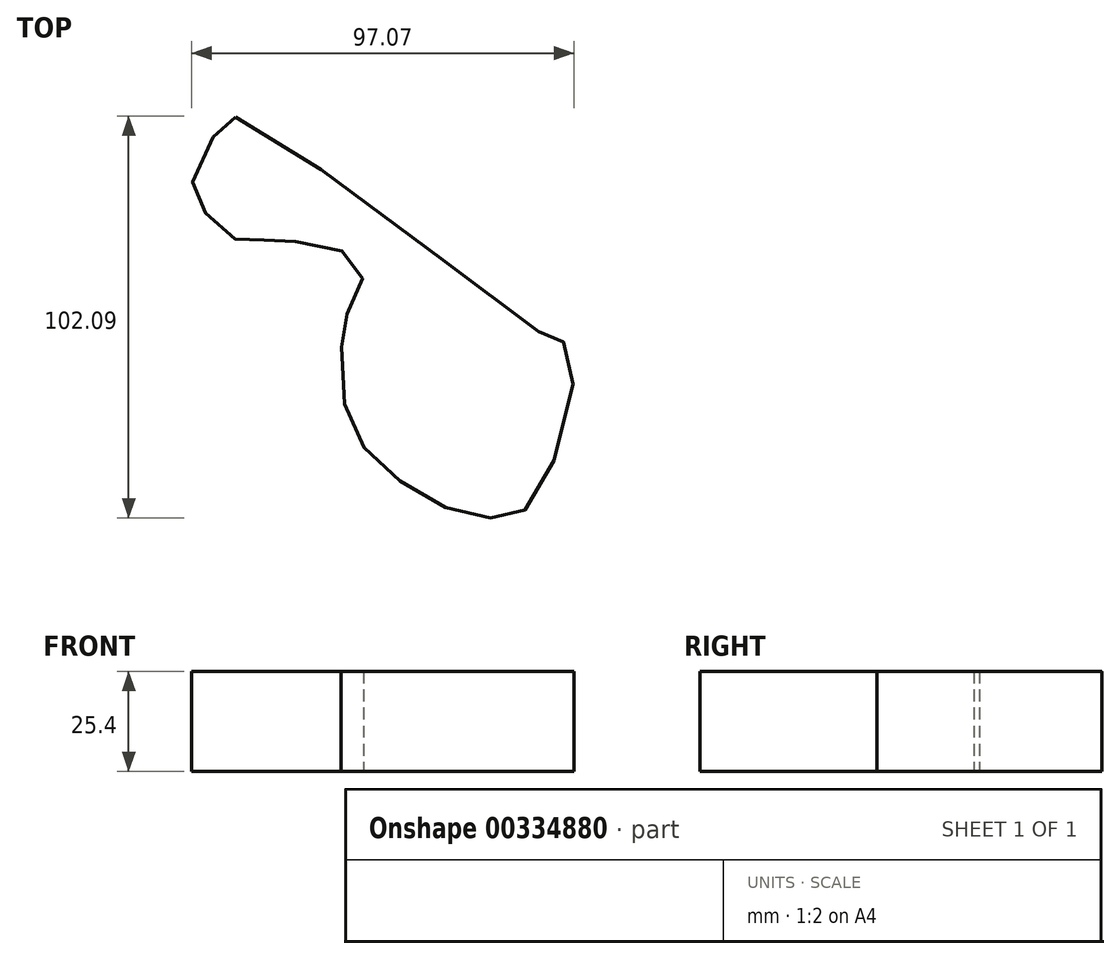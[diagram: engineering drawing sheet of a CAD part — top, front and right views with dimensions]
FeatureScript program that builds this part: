
annotation { "Feature Type Name" : "Feature", "Feature Type Description" : "" }
export const myFeature = defineFeature(function(context is Context, id is Id, definition is map)
    precondition{}
    {
        {
            var Q0;
            Q0=qCreatedBy(makeId("Top.planeOp"),FACE);
            var sketch = newSketch(context, id + "F0", { "sketchPlane" : qUnion([Q0])});
            skFitSpline(sketch, "E0", {"points": [v(-45.93, 48.48) * mm, v(35.54, -8.57) * mm, v(36.45, -8.38) * mm, v(39.55, -11.66) * mm, v(30.98, -47.2) * mm, v(22.24, -53.22) * mm, v(8.02, -50.85) * mm, v(-9.3, -39.73) * mm, v(-17.86, -25.88) * mm, v(-18.6, -4.92) * mm, v(-16.77, 0) * mm, v(-13.85, 11.3) * mm, v(-27.89, 16.22) * mm, v(-37, 17.68) * mm, v(-43.56, 16.4) * mm, v(-51.58, 22.42) * mm, v(-57.05, 29.7) * mm, v(-50.85, 45.02) * mm, v(-45.93, 48.48) * mm]});
            skSolve(sketch);
        }
        {
            var Q0;
            Q0=makeQuery(id+"F0.imprint","IMPRINT",FACE,{"disambiguationData":[TD([[makeQuery(id+"F0.imprint","IMPRINT",EDGE,{"derivedFrom":sQuery(id+"F0.wireOp",EDGE,"E0")}),-1.0]])]});
            extrude(context, id + "F1", {"entities" : qUnion([Q0]), "depth" : 25.4 * mm});
        }
    });
